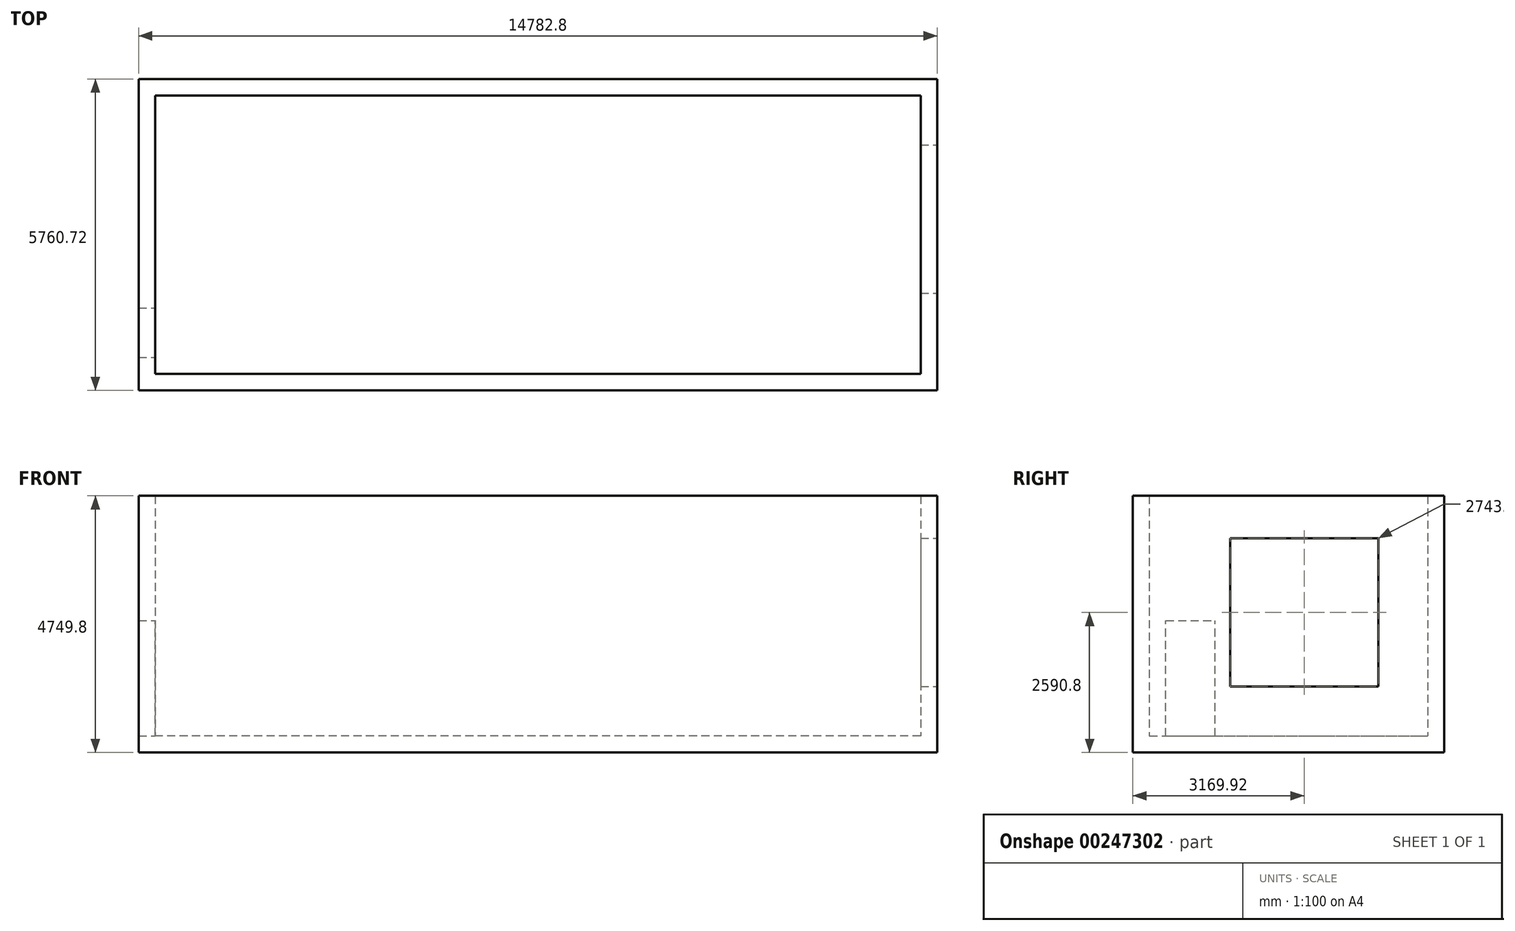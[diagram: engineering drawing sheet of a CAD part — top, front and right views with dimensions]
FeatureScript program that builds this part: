
annotation { "Feature Type Name" : "Feature", "Feature Type Description" : "" }
export const myFeature = defineFeature(function(context is Context, id is Id, definition is map)
    precondition{}
    {
        {
            var Q0;
            Q0=qCreatedBy(makeId("Top.planeOp"),FACE);
            var sketch = newSketch(context, id + "F0", { "sketchPlane" : qUnion([Q0])});
            skLineSegment(sketch, "E0.bottom", {"start": v(7086.6, -2575.56) * mm, "end": v(-7086.6, -2575.56) * mm});
            skLineSegment(sketch, "E0.top", {"start": v(7086.6, 2575.56) * mm, "end": v(-7086.6, 2575.56) * mm});
            skLineSegment(sketch, "E0.left", {"start": v(7086.6, -2575.56) * mm, "end": v(7086.6, 2575.56) * mm});
            skLineSegment(sketch, "E0.right", {"start": v(-7086.6, -2575.56) * mm, "end": v(-7086.6, 2575.56) * mm});
            skPoint(sketch, "E0.middle", {"position": v(0, 0) * mm});
            skLineSegment(sketch, "E1.0", {"start": v(-7391.4, -2880.36) * mm, "end": v(-7391.4, 2880.36) * mm});
            skLineSegment(sketch, "E1.1", {"start": v(7391.4, -2880.36) * mm, "end": v(-7391.4, -2880.36) * mm});
            skLineSegment(sketch, "E1.2", {"start": v(7391.4, -2880.36) * mm, "end": v(7391.4, 2880.36) * mm});
            skLineSegment(sketch, "E1.3", {"start": v(7391.4, 2880.36) * mm, "end": v(-7391.4, 2880.36) * mm});
            skSolve(sketch);
        }
        {
            var Q0;
            Q0=makeQuery(id+"F0.imprint","IMPRINT",FACE,{"disambiguationData":[TD([[makeQuery(id+"F0.imprint","IMPRINT",EDGE,{"derivedFrom":sQuery(id+"F0.wireOp",EDGE,"E0.bottom")}),1.0]])]});
            extrude(context, id + "F1", {"entities" : qUnion([Q0]), "depth" : 4445 * mm, "offsetDistance" : 25.4 * mm});
        }
        {
            var Q0;
            Q0=makeQuery(id+"F1.opExtrude","SWEPT_FACE",FACE,{"disambiguationData":[OSD([sQuery(id+"F0.wireOp",EDGE,"E1.0")])]});
            var sketch = newSketch(context, id + "F2", { "sketchPlane" : qUnion([Q0])});
            skLineSegment(sketch, "E2.bottom", {"start": v(-2880.36, 0) * mm, "end": v(2880.36, 0) * mm});
            skLineSegment(sketch, "E2.top", {"start": v(-2880.36, -304.8) * mm, "end": v(2880.36, -304.8) * mm});
            skLineSegment(sketch, "E2.left", {"start": v(-2880.36, 0) * mm, "end": v(-2880.36, -304.8) * mm});
            skLineSegment(sketch, "E2.right", {"start": v(2880.36, 0) * mm, "end": v(2880.36, -304.8) * mm});
            skSolve(sketch);
        }
        {
            var Q0;
            Q0=makeQuery(id+"F2.imprint","IMPRINT",FACE,{"disambiguationData":[TD([[makeQuery(id+"F2.imprint","IMPRINT",EDGE,{"derivedFrom":sQuery(id+"F2.wireOp",EDGE,"E2.bottom")}),1.0]])]});
            var Q1;
            Q1=makeQuery(id+"F1.opExtrude","SWEPT_FACE",FACE,{"disambiguationData":[OSD([sQuery(id+"F0.wireOp",EDGE,"E1.2")])]});
            extrude(context, id + "F3", {"entities" : qUnion([Q0]), "operationType" : NewBodyOperationType.ADD, "endBound" : BoundingType.UP_TO_SURFACE, "oppositeDirection" : true, "endBoundEntityFace" : qUnion([Q1]), "depth" : 25.4 * mm});
        }
        {
            var Q0;
            {var subQ0=sQuery(id+"F0.wireOp",EDGE,"E1.2");Q0=makeQuery(id+"F3.boolean.opBoolean","MERGE",FACE,{"derivedFrom":[makeQuery(id+"F1.opExtrude","SWEPT_FACE",FACE,{"disambiguationData":[OSD([subQ0])]}),makeQuery(id+"F3.opExtrude","CAP_FACE",FACE,{"disambiguationData":[OSD([subQ0])],"isStart":false})]});}
            var sketch = newSketch(context, id + "F4", { "sketchPlane" : qUnion([Q0])});
            skLineSegment(sketch, "E3.bottom", {"start": v(-1082.04, 3657.6) * mm, "end": v(1661.16, 3657.6) * mm});
            skLineSegment(sketch, "E3.top", {"start": v(-1082.04, 914.4) * mm, "end": v(1661.16, 914.4) * mm});
            skLineSegment(sketch, "E3.left", {"start": v(-1082.04, 3657.6) * mm, "end": v(-1082.04, 914.4) * mm});
            skLineSegment(sketch, "E3.right", {"start": v(1661.16, 3657.6) * mm, "end": v(1661.16, 914.4) * mm});
            skSolve(sketch);
        }
        {
            var Q0;
            Q0 = qSketchRegion(id + "F4", true);
            extrude(context, id + "F5", {"entities" : qUnion([Q0]), "operationType" : NewBodyOperationType.REMOVE, "endBound" : BoundingType.UP_TO_NEXT, "oppositeDirection" : true, "depth" : 25.4 * mm});
        }
        {
            var Q0;
            Q0=makeQuery(id+"F1.opExtrude","SWEPT_FACE",FACE,{"disambiguationData":[OSD([sQuery(id+"F0.wireOp",EDGE,"E0.right")])]});
            var sketch = newSketch(context, id + "F6", { "sketchPlane" : qUnion([Q0])});
            skLineSegment(sketch, "E4.bottom", {"start": v(-2270.76, 0) * mm, "end": v(-1356.36, 0) * mm});
            skLineSegment(sketch, "E4.top", {"start": v(-2270.76, 2133.6) * mm, "end": v(-1356.36, 2133.6) * mm});
            skLineSegment(sketch, "E4.left", {"start": v(-2270.76, 0) * mm, "end": v(-2270.76, 2133.6) * mm});
            skLineSegment(sketch, "E4.right", {"start": v(-1356.36, 0) * mm, "end": v(-1356.36, 2133.6) * mm});
            skSolve(sketch);
        }
        {
            var Q0;
            Q0 = qSketchRegion(id + "F6", true);
            extrude(context, id + "F7", {"entities" : qUnion([Q0]), "operationType" : NewBodyOperationType.REMOVE, "endBound" : BoundingType.UP_TO_NEXT, "oppositeDirection" : true, "depth" : 25.4 * mm});
        }
    });
